# Revit family: BLAUBERG-CIVIC_EC_LB500
name_source: partatom
category: Mechanical Equipment
units: mm (PartAtom-declared; Revit-internal decimal feet)

## family parameters
Always vertical = Yes
Classification = None
Cut with Voids When Loaded = No
OmniClass Number = 23.75.35.14
OmniClass Title = Air Handling Units
Part Type = Normal
Room Calculation Point = No
Round Connector Dimension = Use Diameter
Shared = No
Work Plane-Based = No

## types (4) — shared parameters
Casing Material = Painted Steel White
D1 = 247 mm
Description = Single-room heat recovery air handling unit
Drain Connection Diameter = 8 mm  [stored 0.0262467 ft]
Duct Connection Diameter = 250 mm  [stored 0.82021 ft]
Extract Air Filter = G4x2
Family Version = 1.0
Grid Material = Grid Cross
H = 2162 mm  [stored 7.09318 ft]
H1 = 1833 mm  [stored 6.01378 ft]
H2 = 328 mm  [stored 1.07612 ft]
Hb = 100 mm  [stored 0.328084 ft]
Hc = 2062 mm  [stored 6.76509 ft]
Heat Exchanger Material = polystyrene
Heat Exchanger Type = counter-flow
Heat recovery efficiency (%) = 75..94
Ht = 13 mm
L = 535 mm  [stored 1.75525 ft]
L1 = 585 mm  [stored 1.91929 ft]
Load Classification = HVAC
Maintenance Zone Front Depth = 800 mm  [stored 2.62467 ft]
Maintenance Zone Material = Maintenance Zone
Maintenance Zone Side Depth = 350 mm  [stored 1.14829 ft]
Manufacturer = Blauberg
Maximum Air Flow = 580 m³/h
Maximum Unit Current Without Electric Heater = 2 A
Maximum Unit Power Without Electric Heater = 230 W
Number of Poles = 1
Power Factor = 1
RPM (min-1) = 2150
SEC Class = A
Sound Pressure Level at 1 m (dBA) = 33
Sound Pressure Level at 3 m (dBA) = 23
Supply Air Filter = G4+F8
Transported Air Temperature (°C) = –25 …+40
URL = https://blaubergventilatoren.de
Voltage = 230 V
W = 750 mm  [stored 2.46063 ft]
W1 = 290 mm  [stored 0.951444 ft]
W2 = 230 mm  [stored 0.754593 ft]
dL = 5 mm  [stored 0.0164042 ft]
dW = 5 mm  [stored 0.0164042 ft]
elConBack = 75 mm
elConSide = 200 mm  [stored 0.656168 ft]
ofH = 175 mm  [stored 0.574147 ft]
ofLeft = 55 mm  [stored 0.180446 ft]
ofLeftCenter = 375 mm  [stored 1.23031 ft]
ofRight = 55 mm  [stored 0.180446 ft]
ofRightCenter = 375 mm  [stored 1.23031 ft]
ofTopOfCenter = 150 mm
ofW = 640 mm  [stored 2.09974 ft]
osBack = 65 mm  [stored 0.213255 ft]
osH = 240 mm  [stored 0.787402 ft]
osTopOfCenter = 390 mm  [stored 1.27953 ft]
osW = 380 mm

## per-type parameters (varying)
| type | Current | Maximum Unit Current With Electric Heater | Power | Preheater power | Reheater power | Type Comments | Weight |
| CIVIC EC LB 500 S21 | 2 A | 2 A | 230 W | 0 W | 0 W | Single-room heat recovery air handling unit CIVIC EC LB 500 S21 | 191.00 kg |
| CIVIC EC LB 500 S14 | 2 A | 2 A | 230 W | 0 W | 0 W | Single-room heat recovery air handling unit CIVIC EC LB 500 S14 | 191.00 kg |
| CIVIC EC LBE 500 S21 | 8 A | 8 A | 1630 W | 1400 W | 0 W | Single-room heat recovery air handling unit CIVIC EC LBE 500 S21 | 193.00 kg |
| CIVIC EC LBE2 500 S21 | 20 A | 20 A | 4430 W | 1400 W | 2800 W | Single-room heat recovery air handling unit CIVIC EC LBE2 500 S21 | 194.00 kg |

note: column(s) folded — value = type name in every type: Model

note: [stored X ft] marks values corroborated as IEEE doubles in the binary element streams (Revit-internal decimal feet)

## geometry (parser evidence)
native form markers: Sweep x9
no freeform markers — native parametric forms only
